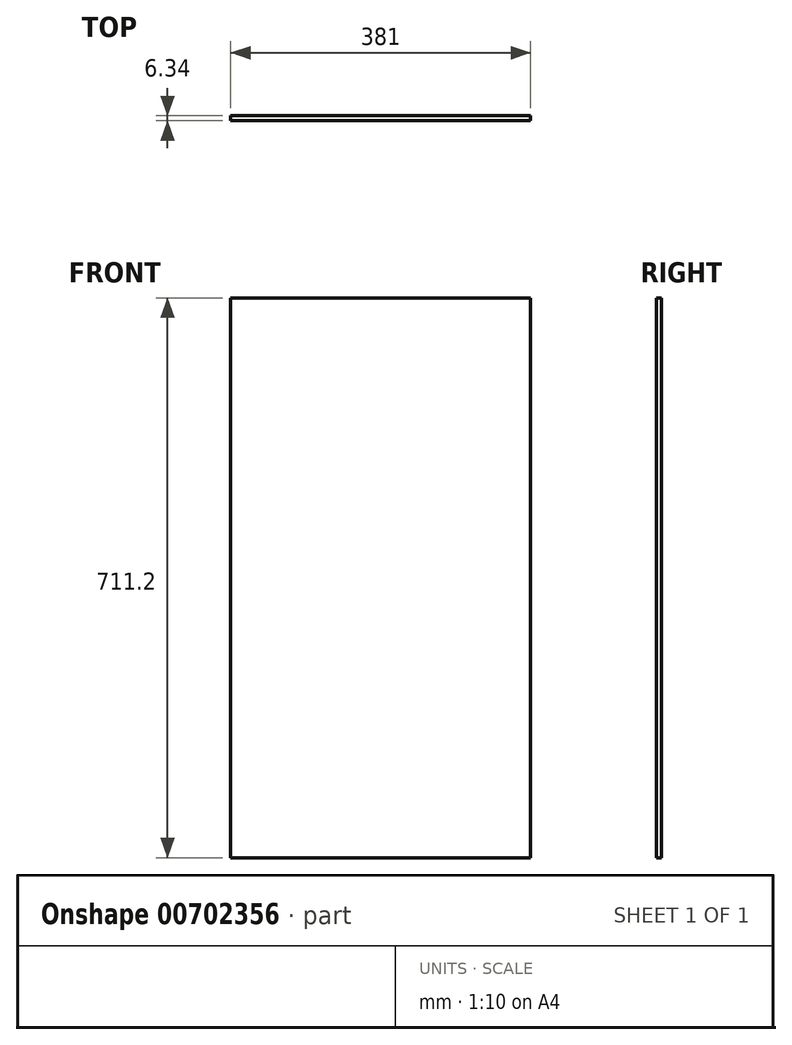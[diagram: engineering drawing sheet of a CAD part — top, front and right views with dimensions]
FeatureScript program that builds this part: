
annotation { "Feature Type Name" : "Feature", "Feature Type Description" : "" }
export const myFeature = defineFeature(function(context is Context, id is Id, definition is map)
    precondition{}
    {
        {
            var Q0;
            Q0=qCreatedBy(makeId("Front.planeOp"),FACE);
            var sketch = newSketch(context, id + "F0", { "sketchPlane" : qUnion([Q0])});
            skLineSegment(sketch, "E0.bottom", {"start": v(-190.5, 355.6) * mm, "end": v(190.5, 355.6) * mm});
            skLineSegment(sketch, "E0.top", {"start": v(-190.5, -355.6) * mm, "end": v(190.5, -355.6) * mm});
            skLineSegment(sketch, "E0.left", {"start": v(-190.5, 355.6) * mm, "end": v(-190.5, -355.6) * mm});
            skLineSegment(sketch, "E0.right", {"start": v(190.5, 355.6) * mm, "end": v(190.5, -355.6) * mm});
            skPoint(sketch, "E0.middle", {"position": v(0, 0) * mm});
            skSolve(sketch);
        }
        {
            var Q0;
            Q0=makeQuery(id+"F0.imprint","IMPRINT",FACE,{"disambiguationData":[TD([[makeQuery(id+"F0.imprint","IMPRINT",EDGE,{"derivedFrom":sQuery(id+"F0.wireOp",EDGE,"E0.bottom")}),-1.0]])]});
            extrude(context, id + "F1", {"entities" : qUnion([Q0]), "endBound" : BoundingType.SYMMETRIC, "depth" : 6.35 * mm, "offsetDistance" : 25.4 * mm});
        }
    });
